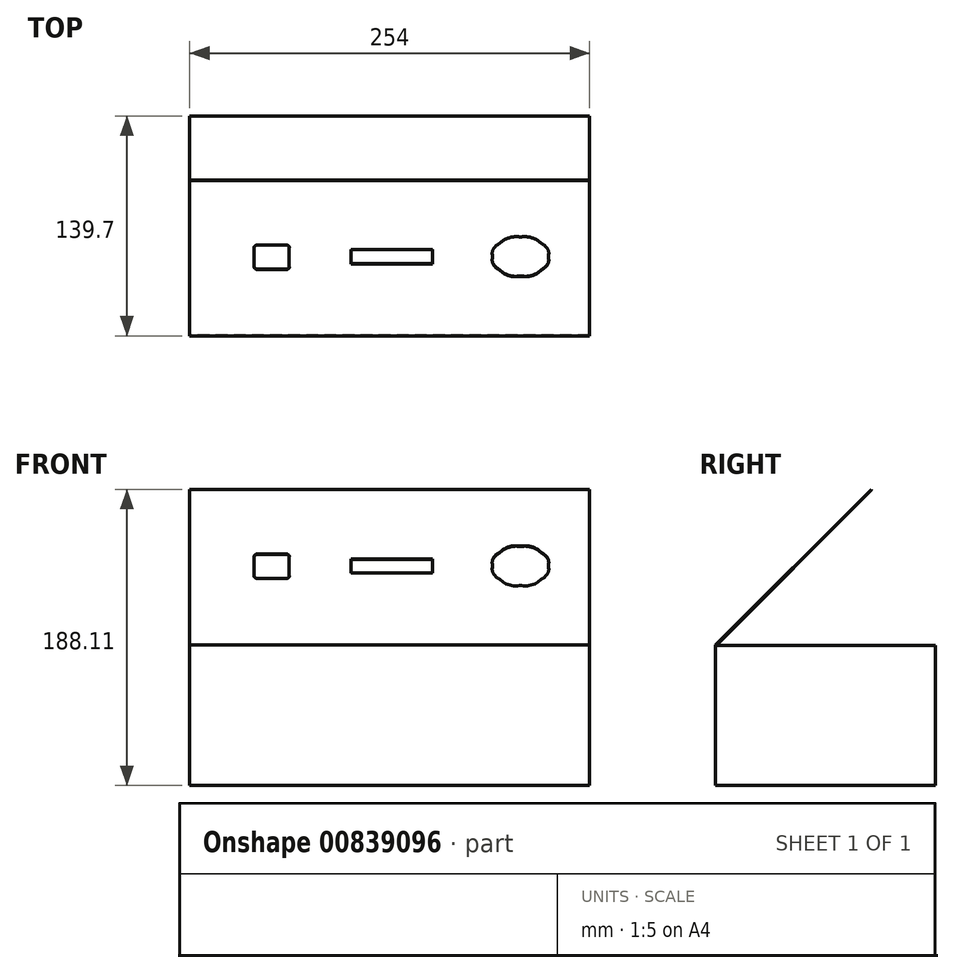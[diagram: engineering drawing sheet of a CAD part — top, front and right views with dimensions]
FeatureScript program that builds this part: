
annotation { "Feature Type Name" : "Feature", "Feature Type Description" : "" }
export const myFeature = defineFeature(function(context is Context, id is Id, definition is map)
    precondition{}
    {
        {
            var Q0;
            Q0=qCreatedBy(makeId("Right.planeOp"),FACE);
            var sketch = newSketch(context, id + "F0", { "sketchPlane" : qUnion([Q0])});
            skLineSegment(sketch, "E0.bottom", {"start": v(0, 0) * mm, "end": v(-139.7, 0) * mm});
            skLineSegment(sketch, "E0.top", {"start": v(0, 88.9) * mm, "end": v(-139.3, 88.9) * mm});
            skLineSegment(sketch, "E0.left", {"start": v(0, 0) * mm, "end": v(0, 88.9) * mm});
            skLineSegment(sketch, "E0.right", {"start": v(-139.7, 0) * mm, "end": v(-139.7, 89.32) * mm});
            skLineSegment(sketch, "E1", {"start": v(-139.7, 89.32) * mm, "end": v(-40.92, 188.1) * mm});
            skLineSegment(sketch, "E2", {"start": v(-40.92, 188.1) * mm, "end": v(-40.63, 187.82) * mm});
            skLineSegment(sketch, "E3", {"start": v(-40.63, 187.82) * mm, "end": v(-139.3, 89.15) * mm});
            skLineSegment(sketch, "E4", {"start": v(-139.3, 88.9) * mm, "end": v(-139.3, 89.15) * mm});
            skLineSegment(sketch, "E5", {"start": v(-139.3, 88.9) * mm, "end": v(-139.7, 88.9) * mm, "construction": true});
            skSolve(sketch);
        }
        {
            var Q0;
            Q0=qSketchRegion(id+"F0",true);
            extrude(context, id + "F1", {"entities" : qUnion([Q0]), "endBound" : BoundingType.SYMMETRIC, "depth" : 254 * mm, "offsetDistance" : 25.4 * mm});
        }
        {
            var Q0;
            Q0=makeQuery(id+"F1.opExtrude","SWEPT_FACE",FACE,{"disambiguationData":[OSD([sQuery(id+"F0.wireOp",EDGE,"E1")])]});
            var sketch = newSketch(context, id + "F2", { "sketchPlane" : qUnion([Q0])});
            skLineSegment(sketch, "E6", {"start": v(-63.82, 26.3) * mm, "end": v(-63.82, 43.77) * mm});
            skLineSegment(sketch, "E7", {"start": v(-83.67, 23.92) * mm, "end": v(-66.2, 23.92) * mm});
            skLineSegment(sketch, "E8", {"start": v(-66.2, 46.15) * mm, "end": v(-83.67, 46.15) * mm});
            skLineSegment(sketch, "E9", {"start": v(-86.05, 43.77) * mm, "end": v(-86.05, 26.3) * mm});
            skLineSegment(sketch, "E10", {"start": v(69.07, -34.42) * mm, "end": v(64.96, -34.42) * mm});
            skLineSegment(sketch, "E11", {"start": v(-125.74, -34.42) * mm, "end": v(-125.74, 104.49) * mm, "construction": true});
            skLineSegment(sketch, "E12", {"start": v(-125.74, 104.49) * mm, "end": v(128.26, 104.49) * mm, "construction": true});
            skLineSegment(sketch, "E13", {"start": v(128.26, -34.42) * mm, "end": v(128.26, 104.49) * mm, "construction": true});
            skLineSegment(sketch, "E14", {"start": v(-24.53, 29.08) * mm, "end": v(27.06, 29.08) * mm});
            skLineSegment(sketch, "E15", {"start": v(-24.53, 41.78) * mm, "end": v(-24.53, 29.08) * mm});
            skLineSegment(sketch, "E16", {"start": v(27.06, 41.78) * mm, "end": v(-24.53, 41.78) * mm});
            skLineSegment(sketch, "E17", {"start": v(27.06, 29.08) * mm, "end": v(27.06, 41.78) * mm});
            skLineSegment(sketch, "E18", {"start": v(128.26, -34.42) * mm, "end": v(-125.74, -34.42) * mm, "construction": true});
            skFitSpline(sketch, "E19", {"points": [v(-66.2, 23.92) * mm, v(-65.58, 23.92) * mm, v(-64.96, 24.18) * mm, v(-64.52, 24.62) * mm]});
            skFitSpline(sketch, "E20", {"points": [v(-64.52, 24.62) * mm, v(-64.08, 25.06) * mm, v(-63.82, 25.68) * mm, v(-63.82, 26.3) * mm]});
            skFitSpline(sketch, "E21", {"points": [v(-63.82, 43.77) * mm, v(-63.82, 44.39) * mm, v(-64.08, 45) * mm, v(-64.52, 45.45) * mm]});
            skFitSpline(sketch, "E22", {"points": [v(-64.52, 45.45) * mm, v(-64.96, 45.89) * mm, v(-65.58, 46.15) * mm, v(-66.2, 46.15) * mm]});
            skFitSpline(sketch, "E23", {"points": [v(-83.67, 46.15) * mm, v(-84.3, 46.15) * mm, v(-84.9, 45.89) * mm, v(-85.35, 45.45) * mm, v(-85.8, 45) * mm, v(-86.05, 44.39) * mm, v(-86.05, 43.77) * mm]});
            skFitSpline(sketch, "E24", {"points": [v(-86.05, 26.3) * mm, v(-86.05, 25.68) * mm, v(-85.8, 25.06) * mm, v(-85.35, 24.62) * mm]});
            skFitSpline(sketch, "E25", {"points": [v(-85.35, 24.62) * mm, v(-84.9, 24.18) * mm, v(-84.3, 23.92) * mm, v(-83.67, 23.92) * mm]});
            skFitSpline(sketch, "E26", {"points": [v(83.02, 53.32) * mm, v(78.34, 53.32) * mm, v(73.7, 51.4) * mm, v(70.39, 48.09) * mm]});
            skFitSpline(sketch, "E27", {"points": [v(70.39, 48.09) * mm, v(67.08, 44.78) * mm, v(65.16, 40.13) * mm, v(65.16, 35.46) * mm, v(65.16, 30.78) * mm, v(67.08, 26.13) * mm, v(70.39, 22.83) * mm]});
            skFitSpline(sketch, "E28", {"points": [v(70.39, 22.83) * mm, v(73.7, 19.52) * mm, v(78.34, 17.6) * mm, v(83.02, 17.6) * mm, v(87.7, 17.6) * mm, v(92.34, 19.52) * mm, v(95.64, 22.83) * mm]});
            skFitSpline(sketch, "E29", {"points": [v(95.64, 22.83) * mm, v(98.95, 26.13) * mm, v(100.88, 30.78) * mm, v(100.88, 35.46) * mm, v(100.88, 40.13) * mm, v(98.95, 44.78) * mm, v(95.64, 48.09) * mm]});
            skFitSpline(sketch, "E30", {"points": [v(95.64, 48.09) * mm, v(92.34, 51.4) * mm, v(87.7, 53.32) * mm, v(83.02, 53.32) * mm]});
            skFitSpline(sketch, "E31", {"points": [v(-66.2, 23.92) * mm, v(-65.58, 23.92) * mm, v(-64.96, 24.18) * mm, v(-64.52, 24.62) * mm]});
            skFitSpline(sketch, "E32", {"points": [v(-64.52, 24.62) * mm, v(-64.08, 25.06) * mm, v(-63.82, 25.68) * mm, v(-63.82, 26.3) * mm]});
            skFitSpline(sketch, "E33", {"points": [v(-63.82, 43.77) * mm, v(-63.82, 44.39) * mm, v(-64.08, 45) * mm, v(-64.52, 45.45) * mm]});
            skFitSpline(sketch, "E34", {"points": [v(-64.52, 45.45) * mm, v(-64.96, 45.89) * mm, v(-65.58, 46.15) * mm, v(-66.2, 46.15) * mm]});
            skFitSpline(sketch, "E35", {"points": [v(-83.67, 46.15) * mm, v(-84.3, 46.15) * mm, v(-84.9, 45.89) * mm, v(-85.35, 45.45) * mm, v(-85.8, 45) * mm, v(-86.05, 44.39) * mm, v(-86.05, 43.77) * mm]});
            skFitSpline(sketch, "E36", {"points": [v(-86.05, 26.3) * mm, v(-86.05, 25.68) * mm, v(-85.8, 25.06) * mm, v(-85.35, 24.62) * mm]});
            skFitSpline(sketch, "E37", {"points": [v(-85.35, 24.62) * mm, v(-84.9, 24.18) * mm, v(-84.3, 23.92) * mm, v(-83.67, 23.92) * mm]});
            skSolve(sketch);
        }
        {
            var Q0;
            Q0=qSketchRegion(id+"F2",true);
            var Q1;
            Q1=makeQuery(id+"F1.opExtrude","SWEPT_FACE",FACE,{"disambiguationData":[OSD([sQuery(id+"F0.wireOp",EDGE,"E3")])]});
            extrude(context, id + "F3", {"entities" : qUnion([Q0]), "operationType" : NewBodyOperationType.REMOVE, "endBound" : BoundingType.UP_TO_SURFACE, "oppositeDirection" : true, "depth" : 25.4 * mm, "endBoundEntityFace" : qUnion([Q1]), "offsetDistance" : 25.4 * mm});
        }
    });
